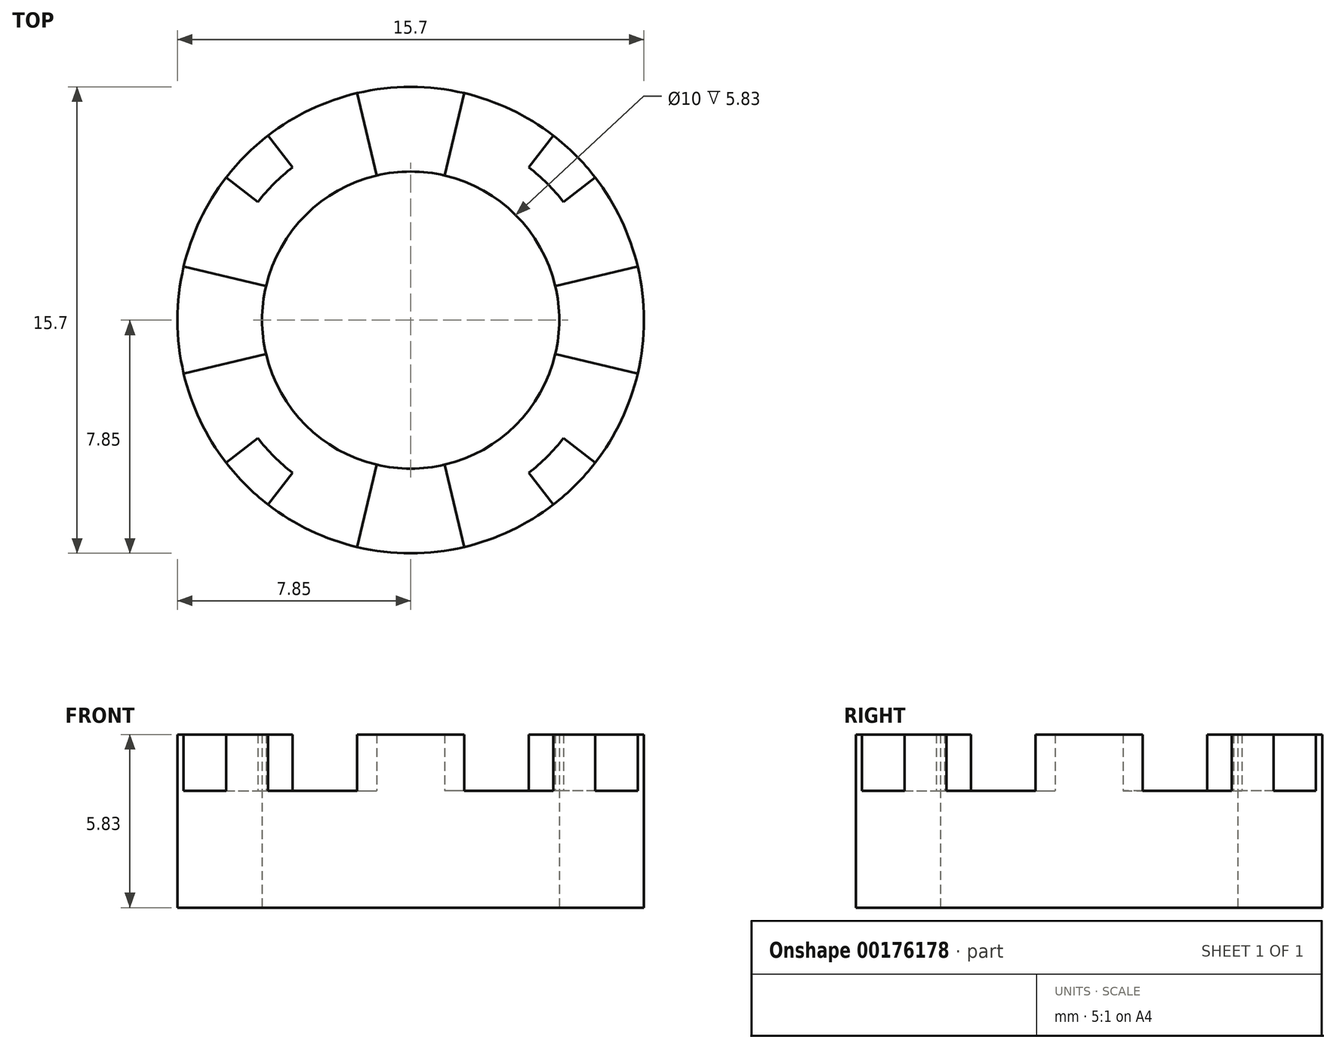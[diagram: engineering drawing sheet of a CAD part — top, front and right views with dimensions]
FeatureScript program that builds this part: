
annotation { "Feature Type Name" : "Feature", "Feature Type Description" : "" }
export const myFeature = defineFeature(function(context is Context, id is Id, definition is map)
    precondition{}
    {
        {
            var Q0;
            Q0=qCreatedBy(makeId("Top.planeOp"),FACE);
            var sketch = newSketch(context, id + "F0", { "sketchPlane" : qUnion([Q0])});
            skArc(sketch, "E0", {"start": v(1.8, 7.64) * mm, "mid": v(0, 7.85) * mm, "end": v(-1.8, 7.64) * mm});
            skArc(sketch, "E1", {"start": v(1.15, 4.87) * mm, "mid": v(0, 5) * mm, "end": v(-1.15, 4.87) * mm});
            skLineSegment(sketch, "E2", {"start": v(0, 0) * mm, "end": v(0, 5) * mm, "construction": true});
            skLineSegment(sketch, "E3", {"start": v(-1.8, 7.64) * mm, "end": v(-1.15, 4.87) * mm});
            skLineSegment(sketch, "E4", {"start": v(1.8, 7.64) * mm, "end": v(1.15, 4.87) * mm});
            skPoint(sketch, "E5", {"position": v(0, 5) * mm});
            skArc(sketch, "E6", {"start": v(5.14, 3.97) * mm, "mid": v(4.6, 4.6) * mm, "end": v(3.97, 5.14) * mm});
            skLineSegment(sketch, "E7", {"start": v(0, 0) * mm, "end": v(4.6, 4.6) * mm, "construction": true});
            skLineSegment(sketch, "E8", {"start": v(4.8, 6.21) * mm, "end": v(3.97, 5.14) * mm});
            skLineSegment(sketch, "E9", {"start": v(6.21, 4.8) * mm, "end": v(5.14, 3.97) * mm});
            skArc(sketch, "E10.trimOffspring", {"start": v(6.21, 4.8) * mm, "mid": v(5.55, 5.55) * mm, "end": v(4.8, 6.21) * mm});
            skSolve(sketch);
        }
        {
            var Q0;
            Q0=makeQuery(id+"F0.imprint","IMPRINT",FACE,{"disambiguationData":[TD([[makeQuery(id+"F0.imprint","IMPRINT",EDGE,{"derivedFrom":sQuery(id+"F0.wireOp",EDGE,"E1")}),-1.0]])]});
            extrude(context, id + "F1", {"entities" : qUnion([Q0]), "depth" : (7.4 - 5.5) * mm});
        }
        {
            var Q0;
            Q0=makeQuery(id+"F0.imprint","IMPRINT",FACE,{"disambiguationData":[TD([[makeQuery(id+"F0.imprint","IMPRINT",EDGE,{"derivedFrom":sQuery(id+"F0.wireOp",EDGE,"E6")}),-1.0]])]});
            var Q1;
            Q1=makeQuery(id+"F1.opExtrude","CAP_FACE",FACE,{"disambiguationData":[OSD([sQuery(id+"F0.wireOp",EDGE,"E1"),sQuery(id+"F0.wireOp",EDGE,"E3"),sQuery(id+"F0.wireOp",EDGE,"E4"),sQuery(id+"F0.wireOp",EDGE,"E0")])],"isStart":false});
            extrude(context, id + "F2", {"entities" : qUnion([Q0]), "endBound" : BoundingType.UP_TO_SURFACE, "endBoundEntityFace" : qUnion([Q1]), "depth" : 25 * mm});
        }
        {
            var Q0;
            Q0=makeQuery(id+"F1.opExtrude","SWEPT_BODY",BODY,{"disambiguationData":[OSD([sQuery(id+"F0.wireOp",EDGE,"E1"),sQuery(id+"F0.wireOp",EDGE,"E3"),sQuery(id+"F0.wireOp",EDGE,"E4"),sQuery(id+"F0.wireOp",EDGE,"E0")])]});
            var Q1;
            Q1=makeQuery(id+"F2.opExtrude","SWEPT_BODY",BODY,{"disambiguationData":[OSD([sQuery(id+"F0.wireOp",EDGE,"E6"),sQuery(id+"F0.wireOp",EDGE,"E8"),sQuery(id+"F0.wireOp",EDGE,"E9"),sQuery(id+"F0.wireOp",EDGE,"E10.trimOffspring")])]});
            var Q2;
            Q2=makeQuery(id+"F1.opExtrude","SWEPT_FACE",FACE,{"disambiguationData":[OSD([sQuery(id+"F0.wireOp",EDGE,"E0")])]});
            circularPattern(context, id + "F3", {"entities" : qUnion([Q0, Q1]), "axis" : qUnion([Q2]), "angle" : 360 * degree, "instanceCount" : 4, "equalSpace" : true, "computeTransformsWithoutBuiltin" : true});
        }
        {
            var Q0;
            Q0=qCreatedBy(makeId("Top.planeOp"),FACE);
            var sketch = newSketch(context, id + "F4", { "sketchPlane" : qUnion([Q0])});
            skCircle(sketch, "E11", {"center": v(0, 0) * mm, "radius": 7.85 * mm});
            skCircle(sketch, "E12", {"center": v(0, 0) * mm, "radius": 5 * mm});
            skSolve(sketch);
        }
        {
            var Q0;
            Q0=makeQuery(id+"F3.opPattern","COPY",FACE,{"derivedFrom":makeQuery(id+"F1.opExtrude","CAP_FACE",FACE,{"disambiguationData":[OSD([sQuery(id+"F0.wireOp",EDGE,"E1"),sQuery(id+"F0.wireOp",EDGE,"E3"),sQuery(id+"F0.wireOp",EDGE,"E4"),sQuery(id+"F0.wireOp",EDGE,"E0")])],"isStart":false}),"instanceName":"2"});
            var sketch = newSketch(context, id + "F5", { "sketchPlane" : qUnion([Q0])});
            skLineSegment(sketch, "E13", {"start": v(0, 0) * mm, "end": v(10.65, -10.65) * mm});
            skLineSegment(sketch, "E14", {"start": v(0, 0) * mm, "end": v(16.85, 0) * mm});
            skLineSegment(sketch, "E15", {"start": v(16.85, 0) * mm, "end": v(10.65, -10.65) * mm});
            skSolve(sketch);
        }
        {
            var Q0;
            Q0=makeQuery(id+"F4.imprint","IMPRINT",FACE,{"disambiguationData":[TD([[makeQuery(id+"F4.imprint","IMPRINT",EDGE,{"derivedFrom":sQuery(id+"F4.wireOp",EDGE,"E11")}),1.0]])]});
            extrude(context, id + "F6", {"entities" : qUnion([Q0]), "operationType" : NewBodyOperationType.ADD, "oppositeDirection" : true, "depth" : 3.93 * mm});
        }
    });
